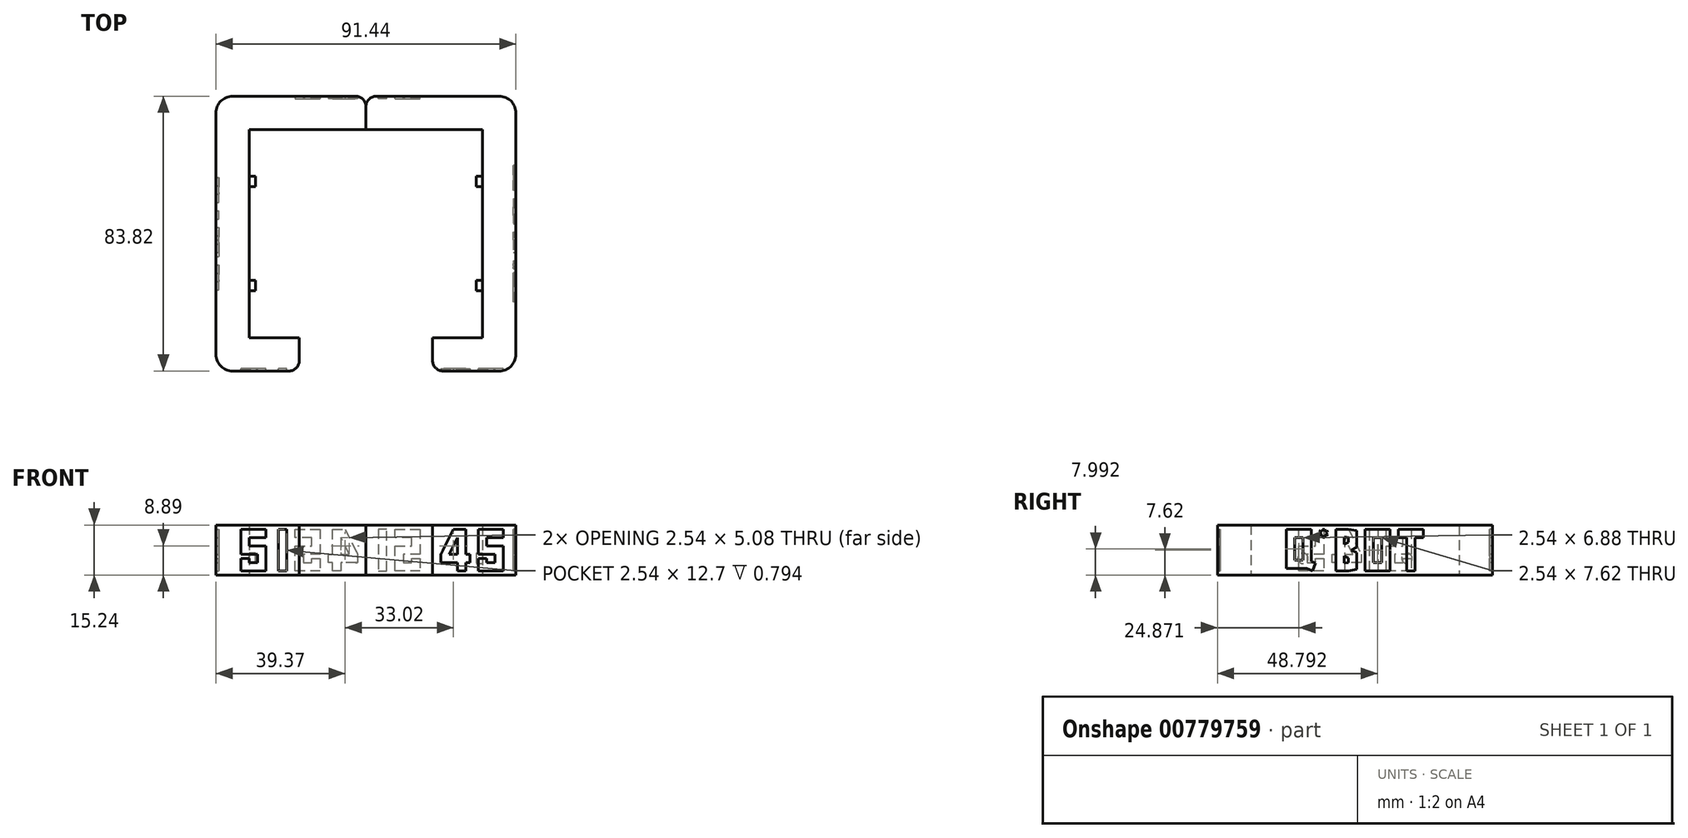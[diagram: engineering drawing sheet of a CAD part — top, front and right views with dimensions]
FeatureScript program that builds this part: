
annotation { "Feature Type Name" : "Feature", "Feature Type Description" : "" }
export const myFeature = defineFeature(function(context is Context, id is Id, definition is map)
    precondition{}
    {
        {
            var Q0;
            Q0=qCreatedBy(makeId("Top.planeOp"),FACE);
            var sketch = newSketch(context, id + "F0", { "sketchPlane" : qUnion([Q0])});
            skLineSegment(sketch, "E0", {"start": v(0, 28.67) * mm, "end": v(0, 38.83) * mm});
            skLineSegment(sketch, "E1", {"start": v(0, 38.83) * mm, "end": v(45.72, 38.83) * mm});
            skLineSegment(sketch, "E2", {"start": v(45.72, 38.83) * mm, "end": v(45.72, -44.99) * mm});
            skLineSegment(sketch, "E3", {"start": v(45.72, -44.99) * mm, "end": v(20.32, -44.99) * mm});
            skLineSegment(sketch, "E4", {"start": v(20.32, -44.99) * mm, "end": v(20.32, -34.83) * mm});
            skLineSegment(sketch, "E5", {"start": v(20.32, -34.83) * mm, "end": v(35.56, -34.83) * mm});
            skLineSegment(sketch, "E6", {"start": v(35.56, -34.83) * mm, "end": v(35.56, 28.67) * mm});
            skLineSegment(sketch, "E7", {"start": v(35.56, 28.67) * mm, "end": v(0, 28.67) * mm});
            skSolve(sketch);
        }
        {
            var Q0;
            Q0=makeQuery(id+"F0.imprint","IMPRINT",FACE,{"disambiguationData":[TD([[makeQuery(id+"F0.imprint","IMPRINT",EDGE,{"derivedFrom":sQuery(id+"F0.wireOp",EDGE,"E0")}),-1.0]])]});
            extrude(context, id + "F1", {"entities" : qUnion([Q0]), "depth" : 15.24 * mm, "offsetDistance" : 25.4 * mm});
        }
        {
            var Q0;
            Q0=makeQuery(id+"F1.opExtrude","SWEPT_FACE",FACE,{"disambiguationData":[OSD([sQuery(id+"F0.wireOp",EDGE,"E6")])]});
            var sketch = newSketch(context, id + "F2", { "sketchPlane" : qUnion([Q0])});
            skCircle(sketch, "E8", {"center": v(-12.8, 5.08) * mm, "radius": 1.59 * mm});
            skPoint(sketch, "E8.centerSnap0", {"position": v(-28.67, 7.62) * mm});
            skCircle(sketch, "E9", {"center": v(18.95, 5.08) * mm, "radius": 1.59 * mm});
            skPoint(sketch, "E9.centerSnap0", {"position": v(34.83, 7.62) * mm});
            skSolve(sketch);
        }
        {
            var Q0;
            Q0=makeQuery(id+"F2.imprint","IMPRINT",FACE,{"disambiguationData":[TD([[makeQuery(id+"F2.imprint","IMPRINT",EDGE,{"derivedFrom":sQuery(id+"F2.wireOp",EDGE,"E8")}),1.0]])]});
            var Q1;
            Q1=makeQuery(id+"F2.imprint","IMPRINT",FACE,{"disambiguationData":[TD([[makeQuery(id+"F2.imprint","IMPRINT",EDGE,{"derivedFrom":sQuery(id+"F2.wireOp",EDGE,"E9")}),1.0]])]});
            extrude(context, id + "F3", {"entities" : qUnion([Q0, Q1]), "operationType" : NewBodyOperationType.ADD, "depth" : 1.9 * mm, "offsetDistance" : 25.4 * mm});
        }
        {
            var Q0;
            Q0=qCreatedBy(makeId("Top.planeOp"),FACE);
            var sketch = newSketch(context, id + "F4", { "sketchPlane" : qUnion([Q0])});
            skLineSegment(sketch, "E10", {"start": v(0, 28.67) * mm, "end": v(-35.56, 28.67) * mm});
            skLineSegment(sketch, "E11", {"start": v(-35.56, 28.67) * mm, "end": v(-35.56, -34.83) * mm});
            skLineSegment(sketch, "E12", {"start": v(-35.56, -34.83) * mm, "end": v(-20.32, -34.83) * mm});
            skLineSegment(sketch, "E13", {"start": v(-20.32, -34.83) * mm, "end": v(-20.32, -44.99) * mm});
            skLineSegment(sketch, "E14", {"start": v(-20.32, -44.99) * mm, "end": v(-45.72, -44.99) * mm});
            skLineSegment(sketch, "E15", {"start": v(-45.72, -44.99) * mm, "end": v(-45.72, 38.83) * mm});
            skLineSegment(sketch, "E16", {"start": v(-45.72, 38.83) * mm, "end": v(0, 38.83) * mm});
            skLineSegment(sketch, "E17", {"start": v(0, 38.83) * mm, "end": v(0, 28.67) * mm});
            skSolve(sketch);
        }
        {
            var Q0;
            Q0=makeQuery(id+"F4.imprint","IMPRINT",FACE,{"disambiguationData":[TD([[makeQuery(id+"F4.imprint","IMPRINT",EDGE,{"derivedFrom":sQuery(id+"F4.wireOp",EDGE,"E10")}),-1.0]])]});
            extrude(context, id + "F5", {"entities" : qUnion([Q0]), "depth" : 15.24 * mm, "offsetDistance" : 25.4 * mm});
        }
        {
            var Q0;
            Q0=makeQuery(id+"F5.opExtrude","SWEPT_FACE",FACE,{"disambiguationData":[OSD([sQuery(id+"F4.wireOp",EDGE,"E11")])]});
            var sketch = newSketch(context, id + "F6", { "sketchPlane" : qUnion([Q0])});
            skCircle(sketch, "E18", {"center": v(-18.95, 5.08) * mm, "radius": 1.59 * mm});
            skPoint(sketch, "E18.centerSnap0", {"position": v(-34.83, 7.62) * mm});
            skCircle(sketch, "E19", {"center": v(12.8, 5.08) * mm, "radius": 1.59 * mm});
            skSolve(sketch);
        }
        {
            var Q0;
            Q0=makeQuery(id+"F6.imprint","IMPRINT",FACE,{"disambiguationData":[TD([[makeQuery(id+"F6.imprint","IMPRINT",EDGE,{"derivedFrom":sQuery(id+"F6.wireOp",EDGE,"E19")}),1.0]])]});
            var Q1;
            Q1=makeQuery(id+"F6.imprint","IMPRINT",FACE,{"disambiguationData":[TD([[makeQuery(id+"F6.imprint","IMPRINT",EDGE,{"derivedFrom":sQuery(id+"F6.wireOp",EDGE,"E18")}),1.0]])]});
            extrude(context, id + "F7", {"entities" : qUnion([Q0, Q1]), "operationType" : NewBodyOperationType.ADD, "depth" : 1.9 * mm, "offsetDistance" : 25.4 * mm});
        }
        {
            var Q0;
            Q0=makeQuery(id+"F1.opExtrude","SWEPT_FACE",FACE,{"disambiguationData":[OSD([sQuery(id+"F0.wireOp",EDGE,"E3")])]});
            var sketch = newSketch(context, id + "F8", { "sketchPlane" : qUnion([Q0])});
            skLineSegment(sketch, "E20", {"start": v(22.86, 6.35) * mm, "end": v(22.86, 3.81) * mm});
            skLineSegment(sketch, "E21", {"start": v(22.86, 3.81) * mm, "end": v(27.94, 3.81) * mm});
            skLineSegment(sketch, "E22", {"start": v(27.94, 3.81) * mm, "end": v(27.94, 1.27) * mm});
            skLineSegment(sketch, "E23", {"start": v(27.94, 1.27) * mm, "end": v(30.48, 1.27) * mm});
            skLineSegment(sketch, "E24", {"start": v(30.48, 1.27) * mm, "end": v(30.48, 3.81) * mm});
            skLineSegment(sketch, "E25", {"start": v(30.48, 3.81) * mm, "end": v(31.75, 3.81) * mm});
            skLineSegment(sketch, "E26", {"start": v(31.75, 3.81) * mm, "end": v(31.75, 6.35) * mm});
            skLineSegment(sketch, "E27", {"start": v(31.75, 6.35) * mm, "end": v(30.48, 6.35) * mm});
            skLineSegment(sketch, "E28", {"start": v(30.48, 6.35) * mm, "end": v(30.48, 13.97) * mm});
            skLineSegment(sketch, "E29", {"start": v(30.48, 13.97) * mm, "end": v(26.67, 13.97) * mm});
            skLineSegment(sketch, "E30", {"start": v(26.67, 13.97) * mm, "end": v(22.86, 6.35) * mm});
            skLineSegment(sketch, "E31", {"start": v(27.94, 6.35) * mm, "end": v(25.4, 6.35) * mm});
            skLineSegment(sketch, "E32", {"start": v(25.4, 6.35) * mm, "end": v(27.94, 11.43) * mm});
            skLineSegment(sketch, "E33", {"start": v(27.94, 11.43) * mm, "end": v(27.94, 6.35) * mm});
            skLineSegment(sketch, "E34", {"start": v(41.91, 13.97) * mm, "end": v(34.3, 13.97) * mm});
            skLineSegment(sketch, "E35", {"start": v(34.3, 13.97) * mm, "end": v(34.3, 6.35) * mm});
            skLineSegment(sketch, "E36", {"start": v(34.3, 6.35) * mm, "end": v(39.37, 6.35) * mm});
            skLineSegment(sketch, "E37", {"start": v(39.37, 6.35) * mm, "end": v(39.37, 3.81) * mm});
            skLineSegment(sketch, "E38", {"start": v(39.37, 3.81) * mm, "end": v(36.83, 3.81) * mm});
            skPoint(sketch, "E38.endSnap0", {"position": v(36.83, 6.35) * mm});
            skLineSegment(sketch, "E39", {"start": v(36.83, 3.81) * mm, "end": v(36.83, 5.08) * mm});
            skPoint(sketch, "E39.endSnap0", {"position": v(39.37, 5.08) * mm});
            skLineSegment(sketch, "E40", {"start": v(36.83, 5.08) * mm, "end": v(34.3, 5.08) * mm});
            skLineSegment(sketch, "E41", {"start": v(34.3, 5.08) * mm, "end": v(34.3, 1.27) * mm});
            skLineSegment(sketch, "E42", {"start": v(34.3, 1.27) * mm, "end": v(41.91, 1.27) * mm});
            skLineSegment(sketch, "E43", {"start": v(41.91, 1.27) * mm, "end": v(41.91, 8.89) * mm});
            skLineSegment(sketch, "E44", {"start": v(41.91, 8.89) * mm, "end": v(36.83, 8.89) * mm});
            skLineSegment(sketch, "E45", {"start": v(36.83, 8.89) * mm, "end": v(36.83, 11.43) * mm});
            skLineSegment(sketch, "E46", {"start": v(36.83, 11.43) * mm, "end": v(41.91, 11.43) * mm});
            skLineSegment(sketch, "E47", {"start": v(41.91, 11.43) * mm, "end": v(41.91, 13.97) * mm});
            skSolve(sketch);
        }
        {
            var Q0;
            Q0=makeQuery(id+"F8.imprint","IMPRINT",FACE,{"disambiguationData":[TD([[makeQuery(id+"F8.imprint","IMPRINT",EDGE,{"derivedFrom":sQuery(id+"F8.wireOp",EDGE,"E20")}),1.0]])]});
            var Q1;
            Q1=makeQuery(id+"F8.imprint","IMPRINT",FACE,{"disambiguationData":[TD([[makeQuery(id+"F8.imprint","IMPRINT",EDGE,{"derivedFrom":sQuery(id+"F8.wireOp",EDGE,"E34")}),1.0]])]});
            extrude(context, id + "F9", {"entities" : qUnion([Q0, Q1]), "operationType" : NewBodyOperationType.REMOVE, "oppositeDirection" : true, "depth" : 0.8 * mm, "offsetDistance" : 25.4 * mm});
        }
        {
            var Q0;
            Q0=makeQuery(id+"F5.opExtrude","SWEPT_FACE",FACE,{"disambiguationData":[OSD([sQuery(id+"F4.wireOp",EDGE,"E14")])]});
            var sketch = newSketch(context, id + "F10", { "sketchPlane" : qUnion([Q0])});
            skLineSegment(sketch, "E48", {"start": v(-24.13, 13.97) * mm, "end": v(-26.67, 13.97) * mm});
            skLineSegment(sketch, "E49", {"start": v(-26.67, 13.97) * mm, "end": v(-26.67, 1.27) * mm});
            skLineSegment(sketch, "E50", {"start": v(-26.67, 1.27) * mm, "end": v(-24.13, 1.27) * mm});
            skLineSegment(sketch, "E51", {"start": v(-24.13, 1.27) * mm, "end": v(-24.13, 13.97) * mm});
            skLineSegment(sketch, "E52", {"start": v(-30.48, 13.97) * mm, "end": v(-38.1, 13.97) * mm});
            skLineSegment(sketch, "E53", {"start": v(-38.1, 13.97) * mm, "end": v(-38.1, 6.35) * mm});
            skLineSegment(sketch, "E54", {"start": v(-38.1, 6.35) * mm, "end": v(-33.02, 6.35) * mm});
            skLineSegment(sketch, "E55", {"start": v(-33.02, 6.35) * mm, "end": v(-33.02, 3.8) * mm});
            skLineSegment(sketch, "E56", {"start": v(-33.02, 3.8) * mm, "end": v(-35.56, 3.8) * mm});
            skLineSegment(sketch, "E57", {"start": v(-35.56, 3.8) * mm, "end": v(-35.56, 5.08) * mm});
            skLineSegment(sketch, "E58", {"start": v(-35.56, 5.08) * mm, "end": v(-38.1, 5.08) * mm});
            skLineSegment(sketch, "E59", {"start": v(-38.1, 5.08) * mm, "end": v(-38.1, 1.27) * mm});
            skLineSegment(sketch, "E60", {"start": v(-38.1, 1.27) * mm, "end": v(-30.48, 1.27) * mm});
            skLineSegment(sketch, "E61", {"start": v(-30.48, 1.27) * mm, "end": v(-30.48, 8.9) * mm});
            skLineSegment(sketch, "E62", {"start": v(-30.48, 8.89) * mm, "end": v(-35.56, 8.89) * mm});
            skLineSegment(sketch, "E63", {"start": v(-35.56, 8.89) * mm, "end": v(-35.56, 11.43) * mm});
            skLineSegment(sketch, "E64", {"start": v(-35.56, 11.43) * mm, "end": v(-30.48, 11.43) * mm});
            skLineSegment(sketch, "E65", {"start": v(-30.48, 11.43) * mm, "end": v(-30.48, 13.97) * mm});
            skSolve(sketch);
        }
        {
            var Q0;
            Q0=makeQuery(id+"F10.imprint","IMPRINT",FACE,{"disambiguationData":[TD([[makeQuery(id+"F10.imprint","IMPRINT",EDGE,{"derivedFrom":sQuery(id+"F10.wireOp",EDGE,"E52")}),1.0]])]});
            var Q1;
            Q1=makeQuery(id+"F10.imprint","IMPRINT",FACE,{"disambiguationData":[TD([[makeQuery(id+"F10.imprint","IMPRINT",EDGE,{"derivedFrom":sQuery(id+"F10.wireOp",EDGE,"E48")}),1.0]])]});
            extrude(context, id + "F11", {"entities" : qUnion([Q0, Q1]), "operationType" : NewBodyOperationType.REMOVE, "oppositeDirection" : true, "depth" : 0.8 * mm, "offsetDistance" : 25.4 * mm});
        }
        {
            var Q0;
            Q0=makeQuery(id+"F5.opExtrude","SWEPT_FACE",FACE,{"disambiguationData":[OSD([sQuery(id+"F4.wireOp",EDGE,"E15")])]});
            var sketch = newSketch(context, id + "F12", { "sketchPlane" : qUnion([Q0])});
            skLineSegment(sketch, "E66", {"start": v(-6.45, 13.97) * mm, "end": v(-14.07, 13.97) * mm});
            skLineSegment(sketch, "E67", {"start": v(-14.07, 13.97) * mm, "end": v(-14.07, 6.35) * mm});
            skLineSegment(sketch, "E68", {"start": v(-14.07, 6.35) * mm, "end": v(-8.99, 6.35) * mm});
            skLineSegment(sketch, "E69", {"start": v(-8.99, 6.35) * mm, "end": v(-8.99, 3.8) * mm});
            skLineSegment(sketch, "E70", {"start": v(-8.99, 3.81) * mm, "end": v(-11.53, 3.81) * mm});
            skLineSegment(sketch, "E71", {"start": v(-11.53, 3.8) * mm, "end": v(-11.53, 5.08) * mm});
            skLineSegment(sketch, "E72", {"start": v(-11.53, 5.08) * mm, "end": v(-14.07, 5.08) * mm});
            skLineSegment(sketch, "E73", {"start": v(-14.07, 5.08) * mm, "end": v(-14.07, 1.27) * mm});
            skLineSegment(sketch, "E74", {"start": v(-14.07, 1.27) * mm, "end": v(-6.45, 1.27) * mm});
            skLineSegment(sketch, "E75", {"start": v(-6.45, 1.27) * mm, "end": v(-6.45, 8.9) * mm});
            skLineSegment(sketch, "E76", {"start": v(-6.45, 8.9) * mm, "end": v(-11.53, 8.9) * mm});
            skLineSegment(sketch, "E77", {"start": v(-11.53, 8.89) * mm, "end": v(-11.53, 11.43) * mm});
            skLineSegment(sketch, "E78", {"start": v(-11.53, 11.43) * mm, "end": v(-6.45, 11.43) * mm});
            skLineSegment(sketch, "E79", {"start": v(-6.45, 11.43) * mm, "end": v(-6.45, 13.97) * mm});
            skLineSegment(sketch, "E80", {"start": v(-3.9, 13.97) * mm, "end": v(-3.9, 1.27) * mm});
            skLineSegment(sketch, "E81", {"start": v(-3.9, 1.27) * mm, "end": v(-1.37, 1.27) * mm});
            skLineSegment(sketch, "E82", {"start": v(-1.37, 1.27) * mm, "end": v(-1.37, 13.97) * mm});
            skLineSegment(sketch, "E83", {"start": v(-1.37, 13.97) * mm, "end": v(-3.9, 13.97) * mm});
            skLineSegment(sketch, "E84", {"start": v(4.98, 13.97) * mm, "end": v(1.17, 6.35) * mm});
            skLineSegment(sketch, "E85", {"start": v(1.17, 6.35) * mm, "end": v(1.17, 3.81) * mm});
            skLineSegment(sketch, "E86", {"start": v(1.17, 3.81) * mm, "end": v(6.25, 3.81) * mm});
            skLineSegment(sketch, "E87", {"start": v(6.25, 3.81) * mm, "end": v(6.25, 1.27) * mm});
            skLineSegment(sketch, "E88", {"start": v(6.25, 1.27) * mm, "end": v(8.8, 1.27) * mm});
            skLineSegment(sketch, "E89", {"start": v(8.8, 1.27) * mm, "end": v(8.8, 3.81) * mm});
            skLineSegment(sketch, "E90", {"start": v(8.8, 3.81) * mm, "end": v(10.06, 3.81) * mm});
            skLineSegment(sketch, "E91", {"start": v(10.06, 3.81) * mm, "end": v(10.06, 6.35) * mm});
            skLineSegment(sketch, "E92", {"start": v(10.06, 6.35) * mm, "end": v(8.8, 6.35) * mm});
            skLineSegment(sketch, "E93", {"start": v(8.8, 6.35) * mm, "end": v(8.8, 13.97) * mm});
            skLineSegment(sketch, "E94", {"start": v(8.8, 13.97) * mm, "end": v(4.98, 13.97) * mm});
            skLineSegment(sketch, "E95", {"start": v(6.25, 6.35) * mm, "end": v(3.71, 6.35) * mm});
            skLineSegment(sketch, "E96", {"start": v(3.71, 6.35) * mm, "end": v(6.25, 11.43) * mm});
            skLineSegment(sketch, "E97", {"start": v(6.25, 11.43) * mm, "end": v(6.25, 6.35) * mm});
            skLineSegment(sketch, "E98", {"start": v(20.22, 13.97) * mm, "end": v(12.6, 13.97) * mm});
            skLineSegment(sketch, "E99", {"start": v(12.6, 13.97) * mm, "end": v(12.6, 6.35) * mm});
            skLineSegment(sketch, "E100", {"start": v(12.6, 6.35) * mm, "end": v(17.68, 6.35) * mm});
            skLineSegment(sketch, "E101", {"start": v(17.68, 6.35) * mm, "end": v(17.68, 3.81) * mm});
            skLineSegment(sketch, "E102", {"start": v(17.68, 3.81) * mm, "end": v(15.14, 3.81) * mm});
            skLineSegment(sketch, "E103", {"start": v(15.14, 3.81) * mm, "end": v(15.14, 5.08) * mm});
            skLineSegment(sketch, "E104", {"start": v(15.14, 5.08) * mm, "end": v(12.6, 5.08) * mm});
            skLineSegment(sketch, "E105", {"start": v(12.6, 5.08) * mm, "end": v(12.6, 1.27) * mm});
            skLineSegment(sketch, "E106", {"start": v(12.6, 1.27) * mm, "end": v(20.22, 1.27) * mm});
            skLineSegment(sketch, "E107", {"start": v(20.22, 1.27) * mm, "end": v(20.22, 8.9) * mm});
            skLineSegment(sketch, "E108", {"start": v(20.22, 8.9) * mm, "end": v(15.14, 8.9) * mm});
            skLineSegment(sketch, "E109", {"start": v(15.14, 8.9) * mm, "end": v(15.14, 11.43) * mm});
            skLineSegment(sketch, "E110", {"start": v(15.14, 11.43) * mm, "end": v(20.22, 11.43) * mm});
            skLineSegment(sketch, "E111", {"start": v(20.22, 11.43) * mm, "end": v(20.22, 13.97) * mm});
            skLineSegment(sketch, "E112", {"start": v(-38.83, 13.97) * mm, "end": v(-14.07, 13.97) * mm});
            skLineSegment(sketch, "E113", {"start": v(44.99, 13.97) * mm, "end": v(20.22, 13.97) * mm});
            skSolve(sketch);
        }
        {
            var Q0;
            Q0=qSketchRegion(id+"F12",true);
            extrude(context, id + "F13", {"entities" : qUnion([Q0]), "operationType" : NewBodyOperationType.REMOVE, "oppositeDirection" : true, "depth" : 0.8 * mm, "offsetDistance" : 25.4 * mm});
        }
        {
            var Q0;
            Q0=makeQuery(id+"F1.opExtrude","SWEPT_FACE",FACE,{"disambiguationData":[OSD([sQuery(id+"F0.wireOp",EDGE,"E1")])]});
            var sketch = newSketch(context, id + "F14", { "sketchPlane" : qUnion([Q0])});
            skLineSegment(sketch, "E114", {"start": v(-8.9, 13.97) * mm, "end": v(-16.51, 13.97) * mm});
            skLineSegment(sketch, "E115", {"start": v(-16.51, 13.97) * mm, "end": v(-16.51, 6.35) * mm});
            skLineSegment(sketch, "E116", {"start": v(-16.51, 6.35) * mm, "end": v(-11.43, 6.35) * mm});
            skLineSegment(sketch, "E117", {"start": v(-11.43, 6.35) * mm, "end": v(-11.43, 3.81) * mm});
            skLineSegment(sketch, "E118", {"start": v(-11.43, 3.81) * mm, "end": v(-13.97, 3.8) * mm});
            skLineSegment(sketch, "E119", {"start": v(-13.97, 3.8) * mm, "end": v(-13.97, 5.08) * mm});
            skLineSegment(sketch, "E120", {"start": v(-13.97, 5.08) * mm, "end": v(-16.51, 5.08) * mm});
            skLineSegment(sketch, "E121", {"start": v(-16.51, 5.08) * mm, "end": v(-16.51, 1.27) * mm});
            skLineSegment(sketch, "E122", {"start": v(-16.51, 1.27) * mm, "end": v(-8.9, 1.27) * mm});
            skLineSegment(sketch, "E123", {"start": v(-8.9, 1.27) * mm, "end": v(-8.9, 8.89) * mm});
            skLineSegment(sketch, "E124", {"start": v(-8.9, 8.9) * mm, "end": v(-13.97, 8.89) * mm});
            skLineSegment(sketch, "E125", {"start": v(-13.97, 8.89) * mm, "end": v(-13.97, 11.43) * mm});
            skLineSegment(sketch, "E126", {"start": v(-13.97, 11.43) * mm, "end": v(-8.9, 11.43) * mm});
            skLineSegment(sketch, "E127", {"start": v(-8.9, 11.43) * mm, "end": v(-8.9, 13.97) * mm});
            skLineSegment(sketch, "E128", {"start": v(-6.35, 13.97) * mm, "end": v(-3.81, 13.97) * mm});
            skLineSegment(sketch, "E129", {"start": v(-3.81, 13.97) * mm, "end": v(-3.81, 1.27) * mm});
            skLineSegment(sketch, "E130", {"start": v(-3.81, 1.27) * mm, "end": v(-6.35, 1.27) * mm});
            skLineSegment(sketch, "E131", {"start": v(-6.35, 1.27) * mm, "end": v(-6.35, 13.97) * mm});
            skSolve(sketch);
        }
        {
            var Q0;
            Q0=qSketchRegion(id+"F14",true);
            extrude(context, id + "F15", {"entities" : qUnion([Q0]), "operationType" : NewBodyOperationType.REMOVE, "oppositeDirection" : true, "depth" : 0.8 * mm, "offsetDistance" : 25.4 * mm});
        }
        {
            var Q0;
            Q0=makeQuery(id+"F5.opExtrude","SWEPT_FACE",FACE,{"disambiguationData":[OSD([sQuery(id+"F4.wireOp",EDGE,"E16")])]});
            var sketch = newSketch(context, id + "F16", { "sketchPlane" : qUnion([Q0])});
            skLineSegment(sketch, "E132", {"start": v(2.54, 6.35) * mm, "end": v(2.54, 3.81) * mm});
            skLineSegment(sketch, "E133", {"start": v(2.54, 3.81) * mm, "end": v(7.62, 3.81) * mm});
            skLineSegment(sketch, "E134", {"start": v(7.62, 3.81) * mm, "end": v(7.62, 1.27) * mm});
            skLineSegment(sketch, "E135", {"start": v(7.62, 1.27) * mm, "end": v(10.16, 1.27) * mm});
            skLineSegment(sketch, "E136", {"start": v(10.16, 1.27) * mm, "end": v(10.16, 3.81) * mm});
            skLineSegment(sketch, "E137", {"start": v(10.16, 3.81) * mm, "end": v(11.43, 3.81) * mm});
            skLineSegment(sketch, "E138", {"start": v(11.43, 3.81) * mm, "end": v(11.43, 6.35) * mm});
            skLineSegment(sketch, "E139", {"start": v(11.43, 6.35) * mm, "end": v(10.16, 6.35) * mm});
            skLineSegment(sketch, "E140", {"start": v(10.16, 6.35) * mm, "end": v(10.16, 13.97) * mm});
            skLineSegment(sketch, "E141", {"start": v(10.16, 13.97) * mm, "end": v(6.35, 13.97) * mm});
            skLineSegment(sketch, "E142", {"start": v(6.35, 13.97) * mm, "end": v(2.54, 6.35) * mm});
            skLineSegment(sketch, "E143", {"start": v(7.62, 6.35) * mm, "end": v(5.08, 6.35) * mm});
            skLineSegment(sketch, "E144", {"start": v(5.08, 6.35) * mm, "end": v(7.62, 11.43) * mm});
            skLineSegment(sketch, "E145", {"start": v(7.62, 11.43) * mm, "end": v(7.62, 6.35) * mm});
            skLineSegment(sketch, "E146", {"start": v(21.6, 13.97) * mm, "end": v(13.97, 13.97) * mm});
            skLineSegment(sketch, "E147", {"start": v(13.97, 13.97) * mm, "end": v(13.97, 6.35) * mm});
            skLineSegment(sketch, "E148", {"start": v(13.97, 6.35) * mm, "end": v(19.05, 6.35) * mm});
            skLineSegment(sketch, "E149", {"start": v(19.05, 6.35) * mm, "end": v(19.05, 3.81) * mm});
            skLineSegment(sketch, "E150", {"start": v(19.05, 3.81) * mm, "end": v(16.51, 3.81) * mm});
            skLineSegment(sketch, "E151", {"start": v(16.51, 3.81) * mm, "end": v(16.51, 5.08) * mm});
            skLineSegment(sketch, "E152", {"start": v(16.51, 5.08) * mm, "end": v(13.97, 5.08) * mm});
            skLineSegment(sketch, "E153", {"start": v(13.97, 5.08) * mm, "end": v(13.97, 1.27) * mm});
            skLineSegment(sketch, "E154", {"start": v(13.97, 1.27) * mm, "end": v(21.59, 1.27) * mm});
            skLineSegment(sketch, "E155", {"start": v(21.59, 1.27) * mm, "end": v(21.59, 8.9) * mm});
            skLineSegment(sketch, "E156", {"start": v(21.59, 8.9) * mm, "end": v(16.51, 8.9) * mm});
            skLineSegment(sketch, "E157", {"start": v(16.51, 8.9) * mm, "end": v(16.51, 11.43) * mm});
            skLineSegment(sketch, "E158", {"start": v(16.51, 11.43) * mm, "end": v(21.59, 11.43) * mm});
            skLineSegment(sketch, "E159", {"start": v(21.59, 11.43) * mm, "end": v(21.59, 13.97) * mm});
            skSolve(sketch);
        }
        {
            var Q0;
            Q0=qSketchRegion(id+"F16",true);
            extrude(context, id + "F17", {"entities" : qUnion([Q0]), "operationType" : NewBodyOperationType.REMOVE, "oppositeDirection" : true, "depth" : 0.8 * mm, "offsetDistance" : 25.4 * mm});
        }
        {
            var Q0;
            Q0=makeQuery(id+"F5.opExtrude","SWEPT_EDGE",EDGE,{"disambiguationData":[OSD([sQuery(id+"F4.wireOp",EDGE,"E15"),sQuery(id+"F4.wireOp",EDGE,"E16")])]});
            var Q1;
            Q1=makeQuery(id+"F5.opExtrude","SWEPT_EDGE",EDGE,{"disambiguationData":[OSD([sQuery(id+"F4.wireOp",EDGE,"E14"),sQuery(id+"F4.wireOp",EDGE,"E15")])]});
            fillet(context, id + "F18", {"entities" : qUnion([Q0, Q1]), "tangentPropagation" : true, "radius" : 5.08 * mm, "defaultsChanged" : true, "vertexSettings" : [], "allowEdgeOverflow" : false});
        }
        {
            var Q0;
            Q0=makeQuery(id+"F1.opExtrude","SWEPT_EDGE",EDGE,{"disambiguationData":[OSD([sQuery(id+"F0.wireOp",EDGE,"E2"),sQuery(id+"F0.wireOp",EDGE,"E3")])]});
            var Q1;
            Q1=makeQuery(id+"F1.opExtrude","SWEPT_EDGE",EDGE,{"disambiguationData":[OSD([sQuery(id+"F0.wireOp",EDGE,"E1"),sQuery(id+"F0.wireOp",EDGE,"E2")])]});
            fillet(context, id + "F19", {"entities" : qUnion([Q0, Q1]), "tangentPropagation" : true, "radius" : 5.08 * mm, "defaultsChanged" : false, "vertexSettings" : [], "allowEdgeOverflow" : false});
        }
        {
            var Q0;
            Q0=makeQuery(id+"F1.opExtrude","SWEPT_EDGE",EDGE,{"disambiguationData":[OSD([sQuery(id+"F0.wireOp",EDGE,"E3"),sQuery(id+"F0.wireOp",EDGE,"E4")])]});
            var Q1;
            Q1=makeQuery(id+"F5.opExtrude","SWEPT_EDGE",EDGE,{"disambiguationData":[OSD([sQuery(id+"F4.wireOp",EDGE,"E13"),sQuery(id+"F4.wireOp",EDGE,"E14")])]});
            var Q2;
            Q2=makeQuery(id+"F1.opExtrude","SWEPT_EDGE",EDGE,{"disambiguationData":[OSD([sQuery(id+"F0.wireOp",EDGE,"E0"),sQuery(id+"F0.wireOp",EDGE,"E1")])]});
            var Q3;
            Q3=makeQuery(id+"F5.opExtrude","SWEPT_EDGE",EDGE,{"disambiguationData":[OSD([sQuery(id+"F4.wireOp",EDGE,"E16"),sQuery(id+"F4.wireOp",EDGE,"E17")])]});
            fillet(context, id + "F20", {"entities" : qUnion([Q0, Q1, Q2, Q3]), "tangentPropagation" : true, "radius" : 3.17 * mm, "defaultsChanged" : true, "vertexSettings" : [], "allowEdgeOverflow" : false});
        }
        {
            var Q0;
            Q0=makeQuery(id+"F9.boolean.opBoolean","COPY",FACE,{"derivedFrom":makeQuery(id+"F9.opExtrude","CAP_FACE",FACE,{"disambiguationData":[OSD([sQuery(id+"F8.wireOp",EDGE,"E20"),sQuery(id+"F8.wireOp",EDGE,"E21"),sQuery(id+"F8.wireOp",EDGE,"E22"),sQuery(id+"F8.wireOp",EDGE,"E23"),sQuery(id+"F8.wireOp",EDGE,"E24"),sQuery(id+"F8.wireOp",EDGE,"E25"),sQuery(id+"F8.wireOp",EDGE,"E26"),sQuery(id+"F8.wireOp",EDGE,"E27"),sQuery(id+"F8.wireOp",EDGE,"E28"),sQuery(id+"F8.wireOp",EDGE,"E29"),sQuery(id+"F8.wireOp",EDGE,"E30"),sQuery(id+"F8.wireOp",EDGE,"E31"),sQuery(id+"F8.wireOp",EDGE,"E32"),sQuery(id+"F8.wireOp",EDGE,"E33")])],"isStart":false})});
            var Q1;
            Q1=makeQuery(id+"F9.boolean.opBoolean","COPY",FACE,{"derivedFrom":makeQuery(id+"F9.opExtrude","CAP_FACE",FACE,{"disambiguationData":[OSD([sQuery(id+"F8.wireOp",EDGE,"E34"),sQuery(id+"F8.wireOp",EDGE,"E35"),sQuery(id+"F8.wireOp",EDGE,"E36"),sQuery(id+"F8.wireOp",EDGE,"E37"),sQuery(id+"F8.wireOp",EDGE,"E38"),sQuery(id+"F8.wireOp",EDGE,"E39"),sQuery(id+"F8.wireOp",EDGE,"E40"),sQuery(id+"F8.wireOp",EDGE,"E41"),sQuery(id+"F8.wireOp",EDGE,"E42"),sQuery(id+"F8.wireOp",EDGE,"E43"),sQuery(id+"F8.wireOp",EDGE,"E44"),sQuery(id+"F8.wireOp",EDGE,"E45"),sQuery(id+"F8.wireOp",EDGE,"E46"),sQuery(id+"F8.wireOp",EDGE,"E47")])],"isStart":false})});
            var Q2;
            Q2=makeQuery(id+"F11.boolean.opBoolean","COPY",FACE,{"derivedFrom":makeQuery(id+"F11.opExtrude","CAP_FACE",FACE,{"disambiguationData":[OSD([sQuery(id+"F10.wireOp",EDGE,"E48"),sQuery(id+"F10.wireOp",EDGE,"E49"),sQuery(id+"F10.wireOp",EDGE,"E50"),sQuery(id+"F10.wireOp",EDGE,"E51")])],"isStart":false})});
            var Q3;
            Q3=makeQuery(id+"F11.boolean.opBoolean","COPY",FACE,{"derivedFrom":makeQuery(id+"F11.opExtrude","CAP_FACE",FACE,{"disambiguationData":[OSD([sQuery(id+"F10.wireOp",EDGE,"E52"),sQuery(id+"F10.wireOp",EDGE,"E53"),sQuery(id+"F10.wireOp",EDGE,"E54"),sQuery(id+"F10.wireOp",EDGE,"E55"),sQuery(id+"F10.wireOp",EDGE,"E56"),sQuery(id+"F10.wireOp",EDGE,"E57"),sQuery(id+"F10.wireOp",EDGE,"E58"),sQuery(id+"F10.wireOp",EDGE,"E59"),sQuery(id+"F10.wireOp",EDGE,"E60"),sQuery(id+"F10.wireOp",EDGE,"E61"),sQuery(id+"F10.wireOp",EDGE,"E62"),sQuery(id+"F10.wireOp",EDGE,"E63"),sQuery(id+"F10.wireOp",EDGE,"E64"),sQuery(id+"F10.wireOp",EDGE,"E65")])],"isStart":false})});
            extrude(context, id + "F21", {"entities" : qUnion([Q0, Q1, Q2, Q3]), "depth" : 0.8 * mm, "offsetDistance" : 25.4 * mm});
        }
        {
            var Q0;
            Q0=makeQuery(id+"F13.boolean.opBoolean","COPY",FACE,{"derivedFrom":makeQuery(id+"F13.opExtrude","CAP_FACE",FACE,{"disambiguationData":[OSD([sQuery(id+"F12.wireOp",EDGE,"E66"),sQuery(id+"F12.wireOp",EDGE,"E67"),sQuery(id+"F12.wireOp",EDGE,"E68"),sQuery(id+"F12.wireOp",EDGE,"E69"),sQuery(id+"F12.wireOp",EDGE,"E70"),sQuery(id+"F12.wireOp",EDGE,"E71"),sQuery(id+"F12.wireOp",EDGE,"E72"),sQuery(id+"F12.wireOp",EDGE,"E73"),sQuery(id+"F12.wireOp",EDGE,"E74"),sQuery(id+"F12.wireOp",EDGE,"E75"),sQuery(id+"F12.wireOp",EDGE,"E76"),sQuery(id+"F12.wireOp",EDGE,"E77"),sQuery(id+"F12.wireOp",EDGE,"E78"),sQuery(id+"F12.wireOp",EDGE,"E79")])],"isStart":false})});
            var Q1;
            Q1=makeQuery(id+"F13.boolean.opBoolean","COPY",FACE,{"derivedFrom":makeQuery(id+"F13.opExtrude","CAP_FACE",FACE,{"disambiguationData":[OSD([sQuery(id+"F12.wireOp",EDGE,"E80"),sQuery(id+"F12.wireOp",EDGE,"E81"),sQuery(id+"F12.wireOp",EDGE,"E82"),sQuery(id+"F12.wireOp",EDGE,"E83")])],"isStart":false})});
            var Q2;
            Q2=makeQuery(id+"F13.boolean.opBoolean","COPY",FACE,{"derivedFrom":makeQuery(id+"F13.opExtrude","CAP_FACE",FACE,{"disambiguationData":[OSD([sQuery(id+"F12.wireOp",EDGE,"E84"),sQuery(id+"F12.wireOp",EDGE,"E85"),sQuery(id+"F12.wireOp",EDGE,"E86"),sQuery(id+"F12.wireOp",EDGE,"E87"),sQuery(id+"F12.wireOp",EDGE,"E88"),sQuery(id+"F12.wireOp",EDGE,"E89"),sQuery(id+"F12.wireOp",EDGE,"E90"),sQuery(id+"F12.wireOp",EDGE,"E91"),sQuery(id+"F12.wireOp",EDGE,"E92"),sQuery(id+"F12.wireOp",EDGE,"E93"),sQuery(id+"F12.wireOp",EDGE,"E94"),sQuery(id+"F12.wireOp",EDGE,"E95"),sQuery(id+"F12.wireOp",EDGE,"E96"),sQuery(id+"F12.wireOp",EDGE,"E97")])],"isStart":false})});
            var Q3;
            Q3=makeQuery(id+"F13.boolean.opBoolean","COPY",FACE,{"derivedFrom":makeQuery(id+"F13.opExtrude","CAP_FACE",FACE,{"disambiguationData":[OSD([sQuery(id+"F12.wireOp",EDGE,"E98"),sQuery(id+"F12.wireOp",EDGE,"E99"),sQuery(id+"F12.wireOp",EDGE,"E100"),sQuery(id+"F12.wireOp",EDGE,"E101"),sQuery(id+"F12.wireOp",EDGE,"E102"),sQuery(id+"F12.wireOp",EDGE,"E103"),sQuery(id+"F12.wireOp",EDGE,"E104"),sQuery(id+"F12.wireOp",EDGE,"E105"),sQuery(id+"F12.wireOp",EDGE,"E106"),sQuery(id+"F12.wireOp",EDGE,"E107"),sQuery(id+"F12.wireOp",EDGE,"E108"),sQuery(id+"F12.wireOp",EDGE,"E109"),sQuery(id+"F12.wireOp",EDGE,"E110"),sQuery(id+"F12.wireOp",EDGE,"E111")])],"isStart":false})});
            extrude(context, id + "F22", {"entities" : qUnion([Q0, Q1, Q2, Q3]), "depth" : 0.8 * mm, "offsetDistance" : 25.4 * mm});
        }
        {
            var Q0;
            Q0=makeQuery(id+"F15.boolean.opBoolean","COPY",FACE,{"derivedFrom":makeQuery(id+"F15.opExtrude","CAP_FACE",FACE,{"disambiguationData":[OSD([sQuery(id+"F14.wireOp",EDGE,"E114"),sQuery(id+"F14.wireOp",EDGE,"E115"),sQuery(id+"F14.wireOp",EDGE,"E116"),sQuery(id+"F14.wireOp",EDGE,"E117"),sQuery(id+"F14.wireOp",EDGE,"E118"),sQuery(id+"F14.wireOp",EDGE,"E119"),sQuery(id+"F14.wireOp",EDGE,"E120"),sQuery(id+"F14.wireOp",EDGE,"E121"),sQuery(id+"F14.wireOp",EDGE,"E122"),sQuery(id+"F14.wireOp",EDGE,"E123"),sQuery(id+"F14.wireOp",EDGE,"E124"),sQuery(id+"F14.wireOp",EDGE,"E125"),sQuery(id+"F14.wireOp",EDGE,"E126"),sQuery(id+"F14.wireOp",EDGE,"E127")])],"isStart":false})});
            var Q1;
            Q1=makeQuery(id+"F15.boolean.opBoolean","COPY",FACE,{"derivedFrom":makeQuery(id+"F15.opExtrude","CAP_FACE",FACE,{"disambiguationData":[OSD([sQuery(id+"F14.wireOp",EDGE,"E128"),sQuery(id+"F14.wireOp",EDGE,"E129"),sQuery(id+"F14.wireOp",EDGE,"E130"),sQuery(id+"F14.wireOp",EDGE,"E131")])],"isStart":false})});
            var Q2;
            Q2=makeQuery(id+"F17.boolean.opBoolean","COPY",FACE,{"derivedFrom":makeQuery(id+"F17.opExtrude","CAP_FACE",FACE,{"disambiguationData":[OSD([sQuery(id+"F16.wireOp",EDGE,"E132"),sQuery(id+"F16.wireOp",EDGE,"E133"),sQuery(id+"F16.wireOp",EDGE,"E134"),sQuery(id+"F16.wireOp",EDGE,"E135"),sQuery(id+"F16.wireOp",EDGE,"E136"),sQuery(id+"F16.wireOp",EDGE,"E137"),sQuery(id+"F16.wireOp",EDGE,"E138"),sQuery(id+"F16.wireOp",EDGE,"E139"),sQuery(id+"F16.wireOp",EDGE,"E140"),sQuery(id+"F16.wireOp",EDGE,"E141"),sQuery(id+"F16.wireOp",EDGE,"E142"),sQuery(id+"F16.wireOp",EDGE,"E143"),sQuery(id+"F16.wireOp",EDGE,"E144"),sQuery(id+"F16.wireOp",EDGE,"E145")])],"isStart":false})});
            var Q3;
            Q3=makeQuery(id+"F17.boolean.opBoolean","COPY",FACE,{"derivedFrom":makeQuery(id+"F17.opExtrude","CAP_FACE",FACE,{"disambiguationData":[OSD([sQuery(id+"F16.wireOp",EDGE,"E146"),sQuery(id+"F16.wireOp",EDGE,"E147"),sQuery(id+"F16.wireOp",EDGE,"E148"),sQuery(id+"F16.wireOp",EDGE,"E149"),sQuery(id+"F16.wireOp",EDGE,"E150"),sQuery(id+"F16.wireOp",EDGE,"E151"),sQuery(id+"F16.wireOp",EDGE,"E152"),sQuery(id+"F16.wireOp",EDGE,"E153"),sQuery(id+"F16.wireOp",EDGE,"E154"),sQuery(id+"F16.wireOp",EDGE,"E155"),sQuery(id+"F16.wireOp",EDGE,"E156"),sQuery(id+"F16.wireOp",EDGE,"E157"),sQuery(id+"F16.wireOp",EDGE,"E158"),sQuery(id+"F16.wireOp",EDGE,"E159")])],"isStart":false})});
            extrude(context, id + "F23", {"entities" : qUnion([Q0, Q1, Q2, Q3]), "depth" : 0.8 * mm, "offsetDistance" : 25.4 * mm});
        }
        {
            var Q0;
            Q0=makeQuery(id+"F21.opExtrude","SWEPT_FACE",FACE,{"disambiguationData":[OSD([sQuery(id+"F8.wireOp",EDGE,"E42")])]});
            var sketch = newSketch(context, id + "F24", { "sketchPlane" : qUnion([Q0])});
            skArc(sketch, "E160", {"start": v(41.91, 44.83) * mm, "mid": v(41.28, 44.95) * mm, "end": v(40.64, 44.99) * mm});
            skSolve(sketch);
        }
        {
            var Q0;
            {var subQ0=sQuery(id+"F24.wireOp",EDGE,"E160");Q0=makeQuery(id+"F24.imprint","IMPRINT",FACE,{"disambiguationData":[TD([[makeQuery(id+"F24.imprint","IMPRINT",EDGE,{"derivedFrom":subQ0}),-1.0]])]});}
            extrude(context, id + "F25", {"entities" : qUnion([Q0]), "operationType" : NewBodyOperationType.REMOVE, "oppositeDirection" : true, "depth" : 25.4 * mm, "offsetDistance" : 25.4 * mm});
        }
        {
            var Q0;
            Q0=makeQuery(id+"F21.opExtrude","SWEPT_FACE",FACE,{"disambiguationData":[OSD([sQuery(id+"F8.wireOp",EDGE,"E21")])]});
            var sketch = newSketch(context, id + "F26", { "sketchPlane" : qUnion([Q0])});
            skArc(sketch, "E161", {"start": v(23.5, 44.99) * mm, "mid": v(23.18, 44.97) * mm, "end": v(22.86, 44.92) * mm});
            skSolve(sketch);
        }
        {
            var Q0;
            {var subQ0=sQuery(id+"F26.wireOp",EDGE,"E161");Q0=makeQuery(id+"F26.imprint","IMPRINT",FACE,{"disambiguationData":[TD([[makeQuery(id+"F26.imprint","IMPRINT",EDGE,{"derivedFrom":subQ0}),-1.0]])]});}
            extrude(context, id + "F27", {"entities" : qUnion([Q0]), "operationType" : NewBodyOperationType.REMOVE, "oppositeDirection" : true, "depth" : 25.4 * mm, "offsetDistance" : 25.4 * mm});
        }
        {
            var Q0;
            Q0=makeQuery(id+"F23.opExtrude","SWEPT_FACE",FACE,{"disambiguationData":[OSD([sQuery(id+"F16.wireOp",EDGE,"E133")])]});
            var sketch = newSketch(context, id + "F28", { "sketchPlane" : qUnion([Q0])});
            skArc(sketch, "E162", {"start": v(-3.18, -38.83) * mm, "mid": v(-2.86, -38.82) * mm, "end": v(-2.54, -38.77) * mm});
            skSolve(sketch);
        }
        {
            var Q0;
            {var subQ0=sQuery(id+"F28.wireOp",EDGE,"E162");Q0=makeQuery(id+"F28.imprint","IMPRINT",FACE,{"disambiguationData":[TD([[makeQuery(id+"F28.imprint","IMPRINT",EDGE,{"derivedFrom":subQ0}),-1.0]])]});}
            extrude(context, id + "F29", {"entities" : qUnion([Q0]), "operationType" : NewBodyOperationType.REMOVE, "oppositeDirection" : true, "depth" : 25.4 * mm, "offsetDistance" : 25.4 * mm});
        }
        {
            var Q0;
            Q0=makeQuery(id+"F1.opExtrude","SWEPT_FACE",FACE,{"disambiguationData":[OSD([sQuery(id+"F0.wireOp",EDGE,"E2")])]});
            var sketch = newSketch(context, id + "F30", { "sketchPlane" : qUnion([Q0])});
            skCircle(sketch, "E163.cCircle", {"center": v(-12.58, 12.79) * mm, "radius": 1.18 * mm, "construction": true});
            skLineSegment(sketch, "E163.0", {"start": v(-11.4, 13.1) * mm, "end": v(-11.4, 12.47) * mm});
            skLineSegment(sketch, "E163.1", {"start": v(-11.4, 12.47) * mm, "end": v(-11.72, 11.92) * mm});
            skLineSegment(sketch, "E163.2", {"start": v(-11.72, 11.92) * mm, "end": v(-12.27, 11.6) * mm});
            skLineSegment(sketch, "E163.3", {"start": v(-12.27, 11.6) * mm, "end": v(-12.9, 11.6) * mm});
            skLineSegment(sketch, "E163.4", {"start": v(-12.9, 11.6) * mm, "end": v(-13.45, 11.92) * mm});
            skLineSegment(sketch, "E163.5", {"start": v(-13.45, 11.92) * mm, "end": v(-13.77, 12.47) * mm});
            skLineSegment(sketch, "E163.6", {"start": v(-13.77, 12.47) * mm, "end": v(-13.77, 13.1) * mm});
            skLineSegment(sketch, "E163.7", {"start": v(-13.77, 13.1) * mm, "end": v(-13.45, 13.65) * mm});
            skLineSegment(sketch, "E163.8", {"start": v(-13.45, 13.65) * mm, "end": v(-12.9, 13.97) * mm});
            skLineSegment(sketch, "E163.9", {"start": v(-12.9, 13.97) * mm, "end": v(-12.27, 13.97) * mm});
            skLineSegment(sketch, "E163.10", {"start": v(-12.27, 13.97) * mm, "end": v(-11.72, 13.65) * mm});
            skLineSegment(sketch, "E163.11", {"start": v(-11.72, 13.65) * mm, "end": v(-11.4, 13.1) * mm});
            skPoint(sketch, "E163.0.midPoint", {"position": v(-11.4, 12.79) * mm});
            skLineSegment(sketch, "E164", {"start": v(-12.9, 13.97) * mm, "end": v(-12.9, 13.34) * mm});
            skLineSegment(sketch, "E165", {"start": v(-12.9, 13.34) * mm, "end": v(-13.45, 13.65) * mm});
            skLineSegment(sketch, "E166", {"start": v(-13.77, 13.1) * mm, "end": v(-13.22, 12.79) * mm});
            skPoint(sketch, "E166.endSnap0", {"position": v(-13.77, 12.79) * mm});
            skLineSegment(sketch, "E167", {"start": v(-13.22, 12.79) * mm, "end": v(-13.77, 12.47) * mm});
            skLineSegment(sketch, "E168", {"start": v(-13.45, 11.92) * mm, "end": v(-12.9, 12.24) * mm});
            skLineSegment(sketch, "E169", {"start": v(-12.9, 12.24) * mm, "end": v(-12.9, 11.6) * mm});
            skLineSegment(sketch, "E170", {"start": v(-12.27, 11.6) * mm, "end": v(-12.27, 12.24) * mm});
            skLineSegment(sketch, "E171", {"start": v(-12.27, 12.24) * mm, "end": v(-11.72, 11.92) * mm});
            skLineSegment(sketch, "E172", {"start": v(-11.4, 12.47) * mm, "end": v(-11.95, 12.79) * mm});
            skLineSegment(sketch, "E173", {"start": v(-11.95, 12.79) * mm, "end": v(-11.4, 13.1) * mm});
            skLineSegment(sketch, "E174", {"start": v(-11.72, 13.65) * mm, "end": v(-12.27, 13.34) * mm});
            skLineSegment(sketch, "E175", {"start": v(-12.27, 13.34) * mm, "end": v(-12.27, 13.97) * mm});
            skLineSegment(sketch, "E176", {"start": v(-8.86, 13.97) * mm, "end": v(-8.86, 1.27) * mm});
            skLineSegment(sketch, "E177", {"start": v(-8.86, 1.27) * mm, "end": v(-5.05, 1.27) * mm});
            skLineSegment(sketch, "E178", {"start": v(-5.05, 1.27) * mm, "end": v(-2.55, 1.71) * mm});
            skLineSegment(sketch, "E179", {"start": v(-2.55, 1.71) * mm, "end": v(-2.55, 6.8) * mm});
            skLineSegment(sketch, "E180", {"start": v(-2.55, 6.8) * mm, "end": v(-4.15, 7.62) * mm});
            skLineSegment(sketch, "E181", {"start": v(-4.15, 7.62) * mm, "end": v(-2.55, 8.45) * mm});
            skLineSegment(sketch, "E182", {"start": v(-2.55, 8.45) * mm, "end": v(-2.55, 13.53) * mm});
            skLineSegment(sketch, "E183", {"start": v(-2.55, 13.53) * mm, "end": v(-5.05, 13.97) * mm});
            skLineSegment(sketch, "E184", {"start": v(-5.05, 13.97) * mm, "end": v(-8.86, 13.97) * mm});
            skLineSegment(sketch, "E185", {"start": v(-6.32, 11.61) * mm, "end": v(-6.32, 9.36) * mm});
            skLineSegment(sketch, "E186", {"start": v(-6.32, 9.36) * mm, "end": v(-5.09, 10) * mm});
            skLineSegment(sketch, "E187", {"start": v(-5.09, 10) * mm, "end": v(-5.09, 11.4) * mm});
            skLineSegment(sketch, "E188", {"start": v(-5.09, 11.4) * mm, "end": v(-6.32, 11.61) * mm});
            skLineSegment(sketch, "E189", {"start": v(-6.32, 5.88) * mm, "end": v(-6.32, 3.63) * mm});
            skLineSegment(sketch, "E190", {"start": v(-6.32, 3.63) * mm, "end": v(-5.09, 3.84) * mm});
            skLineSegment(sketch, "E191", {"start": v(-5.09, 3.84) * mm, "end": v(-5.09, 5.25) * mm});
            skLineSegment(sketch, "E192", {"start": v(-5.09, 5.25) * mm, "end": v(-6.32, 5.88) * mm});
            skLineSegment(sketch, "E193", {"start": v(0, 13.97) * mm, "end": v(0, 1.27) * mm});
            skLineSegment(sketch, "E194", {"start": v(0, 1.27) * mm, "end": v(7.61, 1.27) * mm});
            skLineSegment(sketch, "E195", {"start": v(7.61, 1.27) * mm, "end": v(7.61, 13.97) * mm});
            skLineSegment(sketch, "E196", {"start": v(7.61, 13.97) * mm, "end": v(0, 13.97) * mm});
            skLineSegment(sketch, "E197", {"start": v(2.53, 11.43) * mm, "end": v(5.07, 11.43) * mm});
            skLineSegment(sketch, "E198", {"start": v(5.07, 11.43) * mm, "end": v(5.07, 3.81) * mm});
            skLineSegment(sketch, "E199", {"start": v(5.07, 3.81) * mm, "end": v(2.53, 3.81) * mm});
            skLineSegment(sketch, "E200", {"start": v(2.53, 3.81) * mm, "end": v(2.53, 11.43) * mm});
            skLineSegment(sketch, "E201", {"start": v(10.15, 13.97) * mm, "end": v(17.77, 13.97) * mm});
            skLineSegment(sketch, "E202", {"start": v(17.77, 13.97) * mm, "end": v(17.77, 11.43) * mm});
            skLineSegment(sketch, "E203", {"start": v(17.77, 11.43) * mm, "end": v(15.23, 11.43) * mm});
            skLineSegment(sketch, "E204", {"start": v(15.23, 11.43) * mm, "end": v(15.23, 1.27) * mm});
            skLineSegment(sketch, "E205", {"start": v(15.23, 1.27) * mm, "end": v(12.7, 1.27) * mm});
            skLineSegment(sketch, "E206", {"start": v(12.7, 1.27) * mm, "end": v(12.7, 11.43) * mm});
            skLineSegment(sketch, "E207", {"start": v(12.7, 11.43) * mm, "end": v(10.15, 11.43) * mm});
            skLineSegment(sketch, "E208", {"start": v(10.15, 11.43) * mm, "end": v(10.15, 13.97) * mm});
            skLineSegment(sketch, "E209", {"start": v(-16.3, 13.97) * mm, "end": v(-23.93, 13.97) * mm});
            skLineSegment(sketch, "E210", {"start": v(-23.93, 13.97) * mm, "end": v(-23.93, 2.01) * mm});
            skLineSegment(sketch, "E211", {"start": v(-23.93, 2.01) * mm, "end": v(-17.8, 2.01) * mm});
            skLineSegment(sketch, "E212", {"start": v(-17.8, 2.01) * mm, "end": v(-16.02, 1.27) * mm});
            skLineSegment(sketch, "E213", {"start": v(-16.02, 1.27) * mm, "end": v(-15.04, 3.61) * mm});
            skLineSegment(sketch, "E214", {"start": v(-15.04, 3.61) * mm, "end": v(-16.3, 4.14) * mm});
            skLineSegment(sketch, "E215", {"start": v(-16.3, 4.14) * mm, "end": v(-16.3, 13.97) * mm});
            skLineSegment(sketch, "E216", {"start": v(-21.39, 11.43) * mm, "end": v(-18.85, 11.43) * mm});
            skLineSegment(sketch, "E217", {"start": v(-18.85, 11.43) * mm, "end": v(-18.85, 4.55) * mm});
            skLineSegment(sketch, "E218", {"start": v(-18.85, 4.55) * mm, "end": v(-21.39, 4.55) * mm});
            skLineSegment(sketch, "E219", {"start": v(-21.39, 4.55) * mm, "end": v(-21.39, 11.43) * mm});
            skLineSegment(sketch, "E220", {"start": v(-23.93, 13.97) * mm, "end": v(-39.9, 13.97) * mm});
            skLineSegment(sketch, "E221", {"start": v(17.77, 13.97) * mm, "end": v(33.75, 13.97) * mm});
            skSolve(sketch);
        }
        {
            var Q0;
            Q0=makeQuery(id+"F30.imprint","IMPRINT",FACE,{"disambiguationData":[TD([[makeQuery(id+"F30.imprint","IMPRINT",EDGE,{"derivedFrom":sQuery(id+"F30.wireOp",EDGE,"E209")}),1.0]])]});
            var Q1;
            Q1=makeQuery(id+"F30.imprint","IMPRINT",FACE,{"disambiguationData":[TD([[makeQuery(id+"F30.imprint","IMPRINT",EDGE,{"derivedFrom":sQuery(id+"F30.wireOp",EDGE,"E163.1")}),-1.0]])]});
            var Q2;
            Q2=makeQuery(id+"F30.imprint","IMPRINT",FACE,{"disambiguationData":[TD([[makeQuery(id+"F30.imprint","IMPRINT",EDGE,{"derivedFrom":sQuery(id+"F30.wireOp",EDGE,"E176")}),1.0]])]});
            var Q3;
            Q3=makeQuery(id+"F30.imprint","IMPRINT",FACE,{"disambiguationData":[TD([[makeQuery(id+"F30.imprint","IMPRINT",EDGE,{"derivedFrom":sQuery(id+"F30.wireOp",EDGE,"E193")}),1.0]])]});
            var Q4;
            Q4=makeQuery(id+"F30.imprint","IMPRINT",FACE,{"disambiguationData":[TD([[makeQuery(id+"F30.imprint","IMPRINT",EDGE,{"derivedFrom":sQuery(id+"F30.wireOp",EDGE,"E201")}),-1.0]])]});
            extrude(context, id + "F31", {"entities" : qUnion([Q0, Q1, Q2, Q3, Q4]), "operationType" : NewBodyOperationType.REMOVE, "oppositeDirection" : true, "depth" : 0.8 * mm, "offsetDistance" : 25.4 * mm});
        }
        {
            var Q0;
            Q0=makeQuery(id+"F31.boolean.opBoolean","COPY",FACE,{"derivedFrom":makeQuery(id+"F31.opExtrude","CAP_FACE",FACE,{"disambiguationData":[OSD([sQuery(id+"F30.wireOp",EDGE,"E209"),sQuery(id+"F30.wireOp",EDGE,"E210"),sQuery(id+"F30.wireOp",EDGE,"E211"),sQuery(id+"F30.wireOp",EDGE,"E212"),sQuery(id+"F30.wireOp",EDGE,"E213"),sQuery(id+"F30.wireOp",EDGE,"E214"),sQuery(id+"F30.wireOp",EDGE,"E215"),sQuery(id+"F30.wireOp",EDGE,"E216"),sQuery(id+"F30.wireOp",EDGE,"E217"),sQuery(id+"F30.wireOp",EDGE,"E218"),sQuery(id+"F30.wireOp",EDGE,"E219")])],"isStart":false})});
            var Q1;
            Q1=makeQuery(id+"F31.boolean.opBoolean","COPY",FACE,{"derivedFrom":makeQuery(id+"F31.opExtrude","CAP_FACE",FACE,{"disambiguationData":[OSD([sQuery(id+"F30.wireOp",EDGE,"E163.1"),sQuery(id+"F30.wireOp",EDGE,"E163.3"),sQuery(id+"F30.wireOp",EDGE,"E163.5"),sQuery(id+"F30.wireOp",EDGE,"E163.7"),sQuery(id+"F30.wireOp",EDGE,"E163.9"),sQuery(id+"F30.wireOp",EDGE,"E163.11"),sQuery(id+"F30.wireOp",EDGE,"E164"),sQuery(id+"F30.wireOp",EDGE,"E165"),sQuery(id+"F30.wireOp",EDGE,"E166"),sQuery(id+"F30.wireOp",EDGE,"E167"),sQuery(id+"F30.wireOp",EDGE,"E168"),sQuery(id+"F30.wireOp",EDGE,"E169"),sQuery(id+"F30.wireOp",EDGE,"E170"),sQuery(id+"F30.wireOp",EDGE,"E171"),sQuery(id+"F30.wireOp",EDGE,"E172"),sQuery(id+"F30.wireOp",EDGE,"E173"),sQuery(id+"F30.wireOp",EDGE,"E174"),sQuery(id+"F30.wireOp",EDGE,"E175")])],"isStart":false})});
            var Q2;
            Q2=makeQuery(id+"F31.boolean.opBoolean","COPY",FACE,{"derivedFrom":makeQuery(id+"F31.opExtrude","CAP_FACE",FACE,{"disambiguationData":[OSD([sQuery(id+"F30.wireOp",EDGE,"E176"),sQuery(id+"F30.wireOp",EDGE,"E177"),sQuery(id+"F30.wireOp",EDGE,"E178"),sQuery(id+"F30.wireOp",EDGE,"E179"),sQuery(id+"F30.wireOp",EDGE,"E180"),sQuery(id+"F30.wireOp",EDGE,"E181"),sQuery(id+"F30.wireOp",EDGE,"E182"),sQuery(id+"F30.wireOp",EDGE,"E183"),sQuery(id+"F30.wireOp",EDGE,"E184"),sQuery(id+"F30.wireOp",EDGE,"E185"),sQuery(id+"F30.wireOp",EDGE,"E186"),sQuery(id+"F30.wireOp",EDGE,"E187"),sQuery(id+"F30.wireOp",EDGE,"E188"),sQuery(id+"F30.wireOp",EDGE,"E189"),sQuery(id+"F30.wireOp",EDGE,"E190"),sQuery(id+"F30.wireOp",EDGE,"E191"),sQuery(id+"F30.wireOp",EDGE,"E192")])],"isStart":false})});
            var Q3;
            Q3=makeQuery(id+"F31.boolean.opBoolean","COPY",FACE,{"derivedFrom":makeQuery(id+"F31.opExtrude","CAP_FACE",FACE,{"disambiguationData":[OSD([sQuery(id+"F30.wireOp",EDGE,"E193"),sQuery(id+"F30.wireOp",EDGE,"E194"),sQuery(id+"F30.wireOp",EDGE,"E195"),sQuery(id+"F30.wireOp",EDGE,"E196"),sQuery(id+"F30.wireOp",EDGE,"E197"),sQuery(id+"F30.wireOp",EDGE,"E198"),sQuery(id+"F30.wireOp",EDGE,"E199"),sQuery(id+"F30.wireOp",EDGE,"E200")])],"isStart":false})});
            var Q4;
            Q4=makeQuery(id+"F31.boolean.opBoolean","COPY",FACE,{"derivedFrom":makeQuery(id+"F31.opExtrude","CAP_FACE",FACE,{"disambiguationData":[OSD([sQuery(id+"F30.wireOp",EDGE,"E201"),sQuery(id+"F30.wireOp",EDGE,"E202"),sQuery(id+"F30.wireOp",EDGE,"E203"),sQuery(id+"F30.wireOp",EDGE,"E204"),sQuery(id+"F30.wireOp",EDGE,"E205"),sQuery(id+"F30.wireOp",EDGE,"E206"),sQuery(id+"F30.wireOp",EDGE,"E207"),sQuery(id+"F30.wireOp",EDGE,"E208")])],"isStart":false})});
            extrude(context, id + "F32", {"entities" : qUnion([Q0, Q1, Q2, Q3, Q4]), "depth" : 0.8 * mm, "offsetDistance" : 25.4 * mm});
        }
    });
